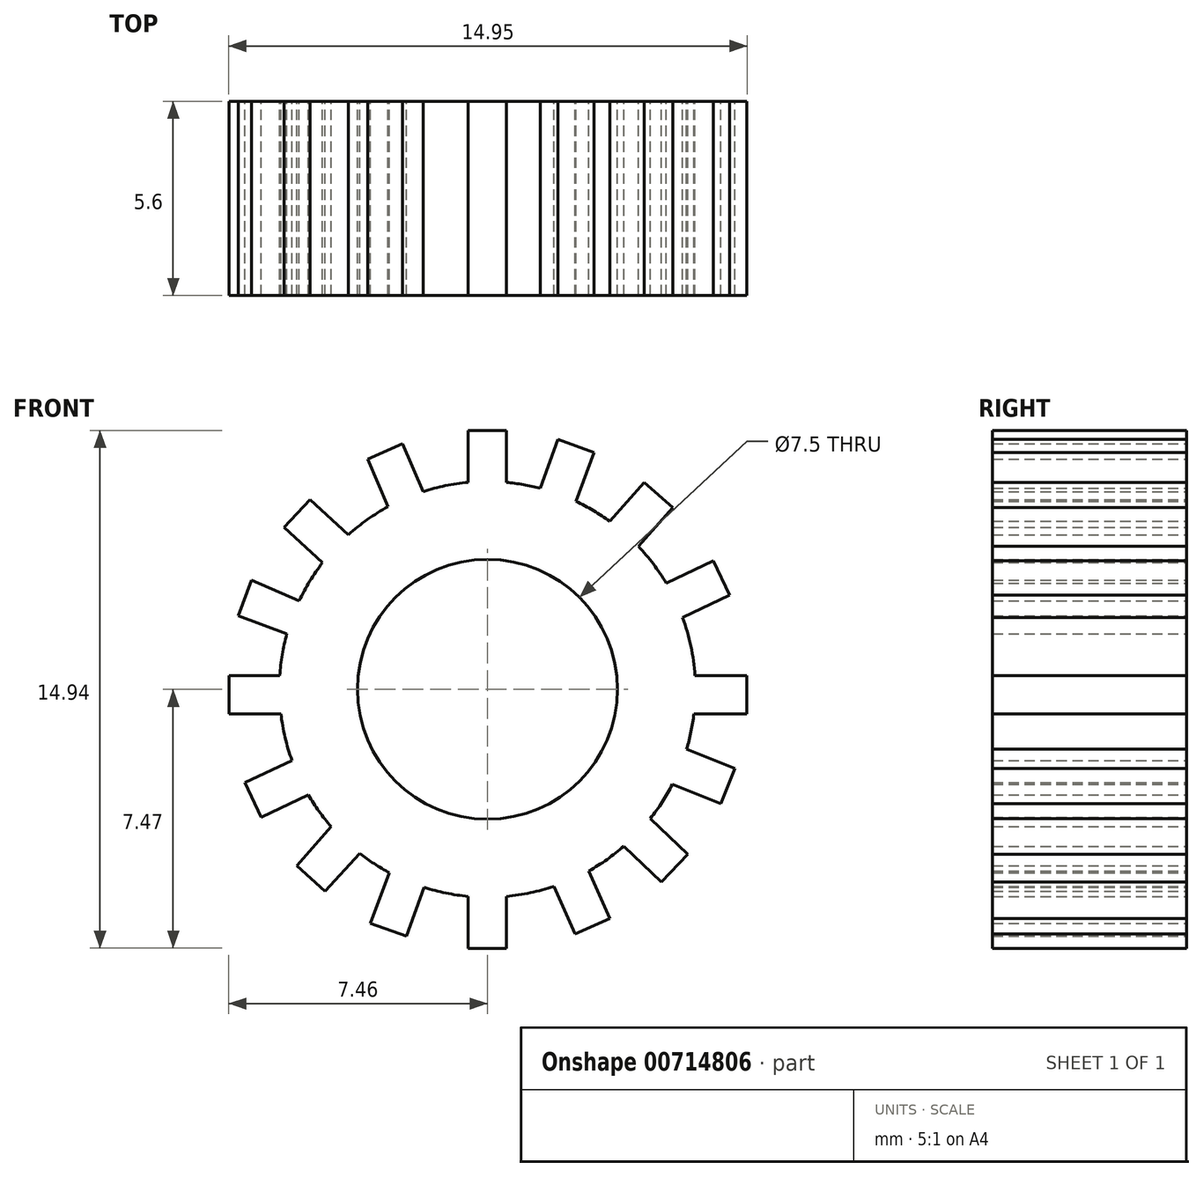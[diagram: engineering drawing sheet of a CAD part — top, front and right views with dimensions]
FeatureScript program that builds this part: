
annotation { "Feature Type Name" : "Feature", "Feature Type Description" : "" }
export const myFeature = defineFeature(function(context is Context, id is Id, definition is map)
    precondition{}
    {
        {
            var Q0;
            Q0=qCreatedBy(makeId("Front.planeOp"),FACE);
            var sketch = newSketch(context, id + "F0", { "sketchPlane" : qUnion([Q0])});
            skArc(sketch, "E0", {"start": v(-2.86, 5.27) * mm, "mid": v(-3.46, 4.9) * mm, "end": v(-4.01, 4.46) * mm});
            skCircle(sketch, "E1", {"center": v(0, 0) * mm, "radius": 3.75 * mm});
            skLineSegment(sketch, "E2", {"start": v(-0.56, 5.97) * mm, "end": v(-0.56, 7.47) * mm});
            skLineSegment(sketch, "E3", {"start": v(-0.56, 7.47) * mm, "end": v(0.54, 7.47) * mm});
            skLineSegment(sketch, "E4", {"start": v(0.54, 7.47) * mm, "end": v(0.54, 5.98) * mm});
            skLineSegment(sketch, "E5", {"start": v(-0.56, -5.97) * mm, "end": v(-0.56, -7.47) * mm});
            skLineSegment(sketch, "E6", {"start": v(-0.56, -7.47) * mm, "end": v(0.54, -7.47) * mm});
            skLineSegment(sketch, "E7", {"start": v(0.54, -7.47) * mm, "end": v(0.54, -5.98) * mm});
            skLineSegment(sketch, "E8", {"start": v(-7.46, 0) * mm, "end": v(-7.46, -0.7) * mm});
            skLineSegment(sketch, "E9", {"start": v(-7.46, -0.7) * mm, "end": v(-5.96, -0.7) * mm});
            skLineSegment(sketch, "E10", {"start": v(-7.46, 0) * mm, "end": v(-7.46, 0.4) * mm});
            skLineSegment(sketch, "E11", {"start": v(-7.46, 0.4) * mm, "end": v(-5.99, 0.4) * mm});
            skLineSegment(sketch, "E12", {"start": v(5.99, 0.4) * mm, "end": v(7.49, 0.4) * mm});
            skLineSegment(sketch, "E13", {"start": v(7.49, 0.4) * mm, "end": v(7.49, -0.7) * mm});
            skLineSegment(sketch, "E14", {"start": v(7.49, -0.7) * mm, "end": v(5.96, -0.7) * mm});
            skLineSegment(sketch, "E15", {"start": v(0, 0) * mm, "end": v(-0.15, -0.16) * mm});
            skLineSegment(sketch, "E16", {"start": v(-4.5, -3.96) * mm, "end": v(-5.5, -5.09) * mm});
            skLineSegment(sketch, "E17", {"start": v(-5.5, -5.09) * mm, "end": v(-4.68, -5.83) * mm});
            skLineSegment(sketch, "E18", {"start": v(-4.68, -5.83) * mm, "end": v(-3.69, -4.73) * mm});
            skLineSegment(sketch, "E19", {"start": v(4.36, 4.12) * mm, "end": v(5.35, 5.25) * mm});
            skLineSegment(sketch, "E20", {"start": v(5.35, 5.25) * mm, "end": v(4.52, 5.98) * mm});
            skLineSegment(sketch, "E21", {"start": v(4.52, 5.98) * mm, "end": v(3.53, 4.85) * mm});
            skLineSegment(sketch, "E22", {"start": v(-4.76, 3.66) * mm, "end": v(-5.86, 4.67) * mm});
            skLineSegment(sketch, "E23", {"start": v(-5.86, 4.67) * mm, "end": v(-5.11, 5.48) * mm});
            skLineSegment(sketch, "E24", {"start": v(-5.11, 5.48) * mm, "end": v(-4.01, 4.46) * mm});
            skLineSegment(sketch, "E25", {"start": v(3.94, -4.53) * mm, "end": v(5.02, -5.56) * mm});
            skLineSegment(sketch, "E26", {"start": v(5.02, -5.56) * mm, "end": v(5.78, -4.77) * mm});
            skLineSegment(sketch, "E27", {"start": v(5.78, -4.77) * mm, "end": v(4.7, -3.73) * mm});
            skLineSegment(sketch, "E28", {"start": v(-5.78, 1.6) * mm, "end": v(-7.19, 2.12) * mm});
            skLineSegment(sketch, "E29", {"start": v(-7.19, 2.12) * mm, "end": v(-6.8, 3.15) * mm});
            skLineSegment(sketch, "E30", {"start": v(-6.8, 3.15) * mm, "end": v(-5.43, 2.55) * mm});
            skLineSegment(sketch, "E31", {"start": v(-2.86, 5.27) * mm, "end": v(-3.46, 6.65) * mm});
            skLineSegment(sketch, "E32", {"start": v(-3.46, 6.65) * mm, "end": v(-2.45, 7.08) * mm});
            skLineSegment(sketch, "E33", {"start": v(-2.45, 7.08) * mm, "end": v(-1.85, 5.7) * mm});
            skLineSegment(sketch, "E34", {"start": v(1.53, 5.8) * mm, "end": v(2.04, 7.21) * mm});
            skLineSegment(sketch, "E35", {"start": v(2.04, 7.21) * mm, "end": v(3.07, 6.84) * mm});
            skLineSegment(sketch, "E36", {"start": v(3.07, 6.84) * mm, "end": v(2.56, 5.43) * mm});
            skLineSegment(sketch, "E37", {"start": v(5.16, 3.07) * mm, "end": v(6.51, 3.71) * mm});
            skLineSegment(sketch, "E38", {"start": v(6.51, 3.71) * mm, "end": v(6.98, 2.72) * mm});
            skLineSegment(sketch, "E39", {"start": v(6.98, 2.72) * mm, "end": v(5.63, 2.07) * mm});
            skLineSegment(sketch, "E40", {"start": v(5.75, -1.72) * mm, "end": v(7.14, -2.28) * mm});
            skLineSegment(sketch, "E41", {"start": v(7.14, -2.28) * mm, "end": v(6.73, -3.3) * mm});
            skLineSegment(sketch, "E42", {"start": v(6.73, -3.3) * mm, "end": v(5.34, -2.74) * mm});
            skLineSegment(sketch, "E43", {"start": v(1.92, -5.68) * mm, "end": v(2.53, -7.06) * mm});
            skLineSegment(sketch, "E44", {"start": v(2.53, -7.06) * mm, "end": v(3.53, -6.6) * mm});
            skLineSegment(sketch, "E45", {"start": v(3.53, -6.6) * mm, "end": v(2.93, -5.24) * mm});
            skLineSegment(sketch, "E46", {"start": v(-3.37, -6.75) * mm, "end": v(-2.34, -7.13) * mm});
            skLineSegment(sketch, "E47", {"start": v(-2.34, -7.13) * mm, "end": v(-1.82, -5.72) * mm});
            skLineSegment(sketch, "E48", {"start": v(-3.37, -6.75) * mm, "end": v(-2.82, -5.3) * mm});
            skLineSegment(sketch, "E49", {"start": v(-5.64, -2.05) * mm, "end": v(-7, -2.7) * mm});
            skLineSegment(sketch, "E50", {"start": v(-7, -2.7) * mm, "end": v(-6.52, -3.69) * mm});
            skLineSegment(sketch, "E51", {"start": v(-6.52, -3.69) * mm, "end": v(-5.17, -3.05) * mm});
            skArc(sketch, "E52.trimOffspring", {"start": v(-0.56, 5.97) * mm, "mid": v(-1.21, 5.88) * mm, "end": v(-1.85, 5.7) * mm});
            skArc(sketch, "E53.trimOffspring", {"start": v(1.53, 5.8) * mm, "mid": v(1.04, 5.9) * mm, "end": v(0.54, 5.98) * mm});
            skArc(sketch, "E54.trimOffspring", {"start": v(3.53, 4.85) * mm, "mid": v(3.06, 5.16) * mm, "end": v(2.56, 5.43) * mm});
            skArc(sketch, "E55.trimOffspring", {"start": v(5.16, 3.07) * mm, "mid": v(4.79, 3.62) * mm, "end": v(4.36, 4.12) * mm});
            skArc(sketch, "E56.trimOffspring", {"start": v(5.99, 0.4) * mm, "mid": v(5.87, 1.25) * mm, "end": v(5.63, 2.07) * mm});
            skArc(sketch, "E57.trimOffspring", {"start": v(5.75, -1.72) * mm, "mid": v(5.88, -1.22) * mm, "end": v(5.96, -0.7) * mm});
            skArc(sketch, "E58.trimOffspring", {"start": v(4.7, -3.73) * mm, "mid": v(5.04, -3.25) * mm, "end": v(5.34, -2.74) * mm});
            skArc(sketch, "E59.trimOffspring", {"start": v(2.93, -5.24) * mm, "mid": v(3.45, -4.9) * mm, "end": v(3.94, -4.53) * mm});
            skArc(sketch, "E60.trimOffspring", {"start": v(0.54, -5.98) * mm, "mid": v(1.24, -5.87) * mm, "end": v(1.92, -5.68) * mm});
            skArc(sketch, "E61.trimOffspring", {"start": v(-1.82, -5.72) * mm, "mid": v(-1.2, -5.88) * mm, "end": v(-0.56, -5.97) * mm});
            skArc(sketch, "E62.trimOffspring", {"start": v(-3.69, -4.73) * mm, "mid": v(-3.27, -5.03) * mm, "end": v(-2.82, -5.3) * mm});
            skArc(sketch, "E63.trimOffspring", {"start": v(-5.17, -3.05) * mm, "mid": v(-4.86, -3.52) * mm, "end": v(-4.5, -3.96) * mm});
            skArc(sketch, "E64.trimOffspring", {"start": v(-5.96, -0.7) * mm, "mid": v(-5.84, -1.39) * mm, "end": v(-5.64, -2.05) * mm});
            skArc(sketch, "E65.trimOffspring", {"start": v(-4.76, 3.66) * mm, "mid": v(-5.12, 3.12) * mm, "end": v(-5.43, 2.55) * mm});
            skArc(sketch, "E66", {"start": v(-5.78, 1.6) * mm, "mid": v(-5.92, 1) * mm, "end": v(-5.99, 0.4) * mm});
            skSolve(sketch);
        }
        {
            var Q0;
            Q0=makeQuery(id+"F0.imprint","IMPRINT",FACE,{"disambiguationData":[TD([[makeQuery(id+"F0.imprint","IMPRINT",EDGE,{"derivedFrom":sQuery(id+"F0.wireOp",EDGE,"E8")}),1.0]])]});
            var Q1;
            {var subQ0=sQuery(id+"F0.wireOp",EDGE,"E28");Q1=makeQuery(id+"F0.imprint","IMPRINT",FACE,{"disambiguationData":[TD([[makeQuery(id+"F0.imprint","IMPRINT",EDGE,{"derivedFrom":subQ0}),-1.0]])]});}
            var Q2;
            {var subQ0=sQuery(id+"F0.wireOp",EDGE,"E22");Q2=makeQuery(id+"F0.imprint","IMPRINT",FACE,{"disambiguationData":[TD([[makeQuery(id+"F0.imprint","IMPRINT",EDGE,{"derivedFrom":subQ0}),-1.0]])]});}
            var Q3;
            {var subQ0=sQuery(id+"F0.wireOp",EDGE,"E31");Q3=makeQuery(id+"F0.imprint","IMPRINT",FACE,{"disambiguationData":[TD([[makeQuery(id+"F0.imprint","IMPRINT",EDGE,{"derivedFrom":subQ0}),-1.0]])]});}
            var Q4;
            {var subQ0=sQuery(id+"F0.wireOp",EDGE,"E2");Q4=makeQuery(id+"F0.imprint","IMPRINT",FACE,{"disambiguationData":[TD([[makeQuery(id+"F0.imprint","IMPRINT",EDGE,{"derivedFrom":subQ0}),-1.0]])]});}
            var Q5;
            {var subQ0=sQuery(id+"F0.wireOp",EDGE,"E34");Q5=makeQuery(id+"F0.imprint","IMPRINT",FACE,{"disambiguationData":[TD([[makeQuery(id+"F0.imprint","IMPRINT",EDGE,{"derivedFrom":subQ0}),-1.0]])]});}
            var Q6;
            {var subQ3=sQuery(id+"F0.wireOp",EDGE,"E19");Q6=makeQuery(id+"F0.imprint","IMPRINT",FACE,{"disambiguationData":[TD([[makeQuery(id+"F0.imprint","IMPRINT",EDGE,{"derivedFrom":subQ3}),1.0]])]});}
            var Q7;
            {var subQ0=sQuery(id+"F0.wireOp",EDGE,"E37");Q7=makeQuery(id+"F0.imprint","IMPRINT",FACE,{"disambiguationData":[TD([[makeQuery(id+"F0.imprint","IMPRINT",EDGE,{"derivedFrom":subQ0}),-1.0]])]});}
            var Q8;
            {var subQ0=sQuery(id+"F0.wireOp",EDGE,"E12");Q8=makeQuery(id+"F0.imprint","IMPRINT",FACE,{"disambiguationData":[TD([[makeQuery(id+"F0.imprint","IMPRINT",EDGE,{"derivedFrom":subQ0}),-1.0]])]});}
            var Q9;
            {var subQ0=sQuery(id+"F0.wireOp",EDGE,"E40");Q9=makeQuery(id+"F0.imprint","IMPRINT",FACE,{"disambiguationData":[TD([[makeQuery(id+"F0.imprint","IMPRINT",EDGE,{"derivedFrom":subQ0}),-1.0]])]});}
            var Q10;
            {var subQ0=sQuery(id+"F0.wireOp",EDGE,"E25");Q10=makeQuery(id+"F0.imprint","IMPRINT",FACE,{"disambiguationData":[TD([[makeQuery(id+"F0.imprint","IMPRINT",EDGE,{"derivedFrom":subQ0}),1.0]])]});}
            var Q11;
            {var subQ0=sQuery(id+"F0.wireOp",EDGE,"E43");Q11=makeQuery(id+"F0.imprint","IMPRINT",FACE,{"disambiguationData":[TD([[makeQuery(id+"F0.imprint","IMPRINT",EDGE,{"derivedFrom":subQ0}),1.0]])]});}
            var Q12;
            {var subQ0=sQuery(id+"F0.wireOp",EDGE,"E5");Q12=makeQuery(id+"F0.imprint","IMPRINT",FACE,{"disambiguationData":[TD([[makeQuery(id+"F0.imprint","IMPRINT",EDGE,{"derivedFrom":subQ0}),1.0]])]});}
            var Q13;
            Q13=makeQuery(id+"F0.imprint","IMPRINT",FACE,{"disambiguationData":[TD([[makeQuery(id+"F0.imprint","IMPRINT",EDGE,{"derivedFrom":sQuery(id+"F0.wireOp",EDGE,"E46")}),1.0]])]});
            var Q14;
            {var subQ0=sQuery(id+"F0.wireOp",EDGE,"E16");Q14=makeQuery(id+"F0.imprint","IMPRINT",FACE,{"disambiguationData":[TD([[makeQuery(id+"F0.imprint","IMPRINT",EDGE,{"derivedFrom":subQ0}),1.0]])]});}
            var Q15;
            {var subQ0=sQuery(id+"F0.wireOp",EDGE,"E49");Q15=makeQuery(id+"F0.imprint","IMPRINT",FACE,{"disambiguationData":[TD([[makeQuery(id+"F0.imprint","IMPRINT",EDGE,{"derivedFrom":subQ0}),1.0]])]});}
            var Q16;
            Q16=makeQuery(id+"F0.imprint","IMPRINT",FACE,{"disambiguationData":[TD([[makeQuery(id+"F0.imprint","IMPRINT",EDGE,{"derivedFrom":sQuery(id+"F0.wireOp",EDGE,"E1")}),-1.0]])]});
            extrude(context, id + "F1", {"entities" : qUnion([Q0, Q1, Q2, Q3, Q4, Q5, Q6, Q7, Q8, Q9, Q10, Q11, Q12, Q13, Q14, Q15, Q16]), "depth" : 5.6 * mm, "offsetDistance" : 25 * mm});
        }
    });
